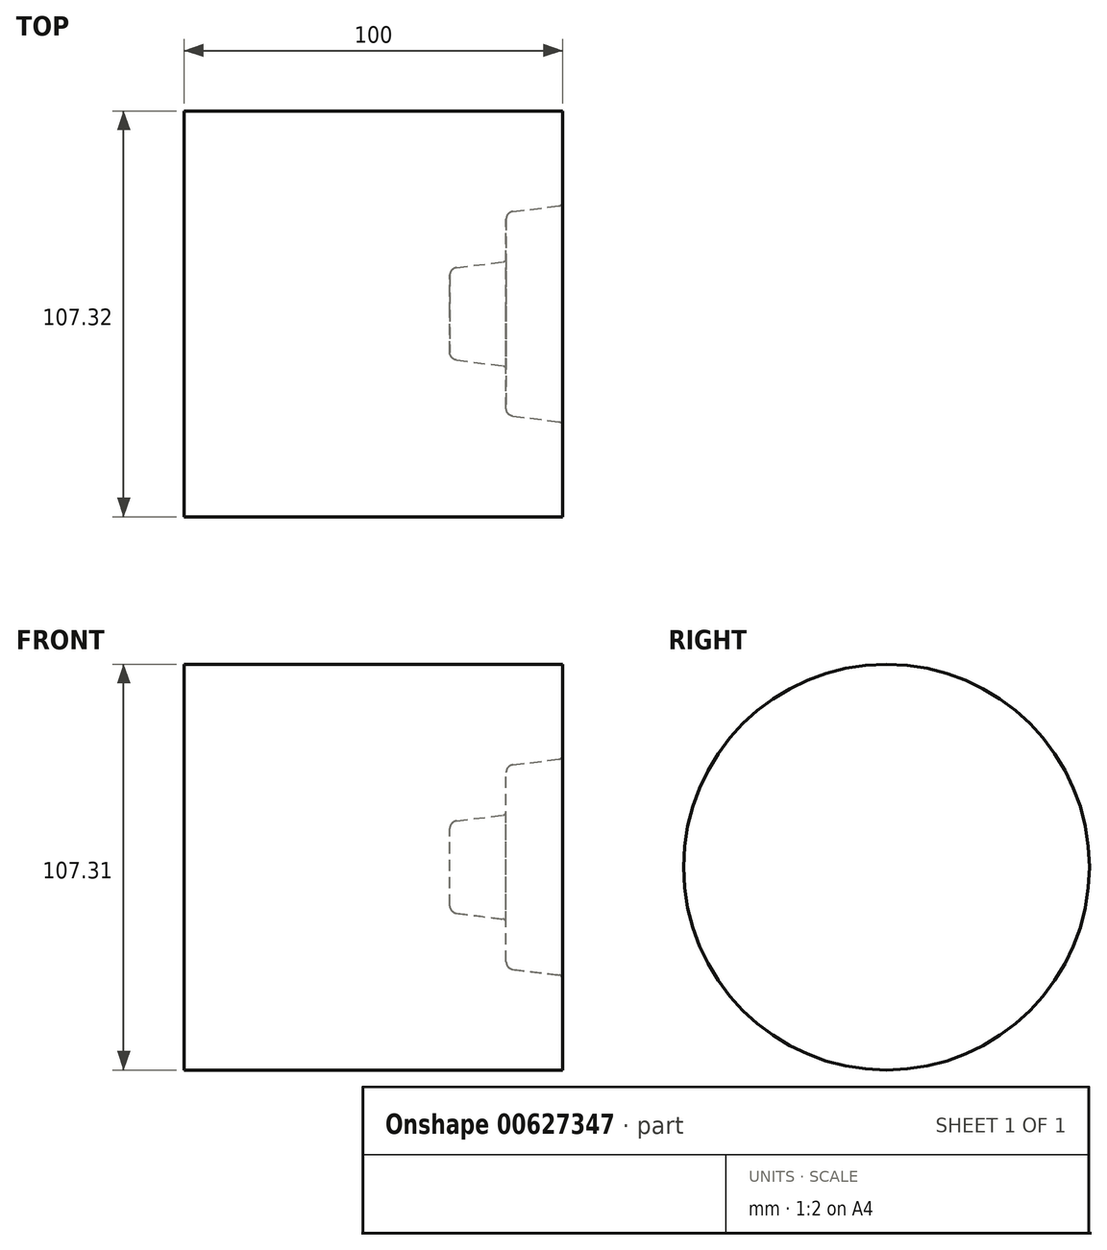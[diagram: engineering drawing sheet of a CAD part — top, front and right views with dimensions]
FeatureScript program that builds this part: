
annotation { "Feature Type Name" : "Feature", "Feature Type Description" : "" }
export const myFeature = defineFeature(function(context is Context, id is Id, definition is map)
    precondition{}
    {
        {
            var Q0;
            Q0=qCreatedBy(makeId("Front.planeOp"),FACE);
            var sketch = newSketch(context, id + "F0", { "sketchPlane" : qUnion([Q0])});
            skLineSegment(sketch, "E0", {"start": v(0, 0) * mm, "end": v(100, 0) * mm});
            skLineSegment(sketch, "E1", {"start": v(100, 0) * mm, "end": v(100, 24.12) * mm});
            skLineSegment(sketch, "E2", {"start": v(99.12, 25.1) * mm, "end": v(86.87, 26.61) * mm});
            skLineSegment(sketch, "E3", {"start": v(85.11, 28.6) * mm, "end": v(85.11, 38.94) * mm});
            skLineSegment(sketch, "E4", {"start": v(84.23, 39.94) * mm, "end": v(71.98, 41.44) * mm});
            skLineSegment(sketch, "E5", {"start": v(70.22, 43.43) * mm, "end": v(70.22, 53.66) * mm});
            skLineSegment(sketch, "E6", {"start": v(70.22, 53.66) * mm, "end": v(0, 53.66) * mm});
            skLineSegment(sketch, "E7", {"start": v(0, 53.66) * mm, "end": v(0, 0) * mm});
            skPoint(sketch, "E8.visualSharp", {"position": v(85.11, 26.83) * mm});
            skArc(sketch, "E8.filletArc", {"start": v(85.11, 28.6) * mm, "mid": v(85.61, 27.27) * mm, "end": v(86.87, 26.61) * mm});
            skPoint(sketch, "E9.visualSharp", {"position": v(70.22, 41.66) * mm});
            skArc(sketch, "E9.filletArc", {"start": v(70.22, 43.43) * mm, "mid": v(70.73, 42.1) * mm, "end": v(71.98, 41.44) * mm});
            skPoint(sketch, "E10.visualSharp", {"position": v(100, 25) * mm});
            skArc(sketch, "E10.filletArc", {"start": v(100, 24.12) * mm, "mid": v(99.75, 24.78) * mm, "end": v(99.12, 25.1) * mm});
            skPoint(sketch, "E11.visualSharp", {"position": v(85.11, 39.83) * mm});
            skArc(sketch, "E11.filletArc", {"start": v(85.11, 38.94) * mm, "mid": v(84.86, 39.6) * mm, "end": v(84.23, 39.94) * mm});
            skSolve(sketch);
        }
        {
            var Q0;
            Q0=makeQuery(id+"F0.imprint","IMPRINT",FACE,{"disambiguationData":[TD([[makeQuery(id+"F0.imprint","IMPRINT",EDGE,{"derivedFrom":sQuery(id+"F0.wireOp",EDGE,"E0")}),1.0]])]});
            var Q1;
            Q1=sQuery(id+"F0.wireOp",EDGE,"E6");
            revolve(context, id + "F1", {"surfaceOperationType" : NewSurfaceOperationType.NEW, "entities" : qUnion([Q0]), "axis" : qUnion([Q1]), "revolveType" : RevolveType.FULL});
        }
    });
